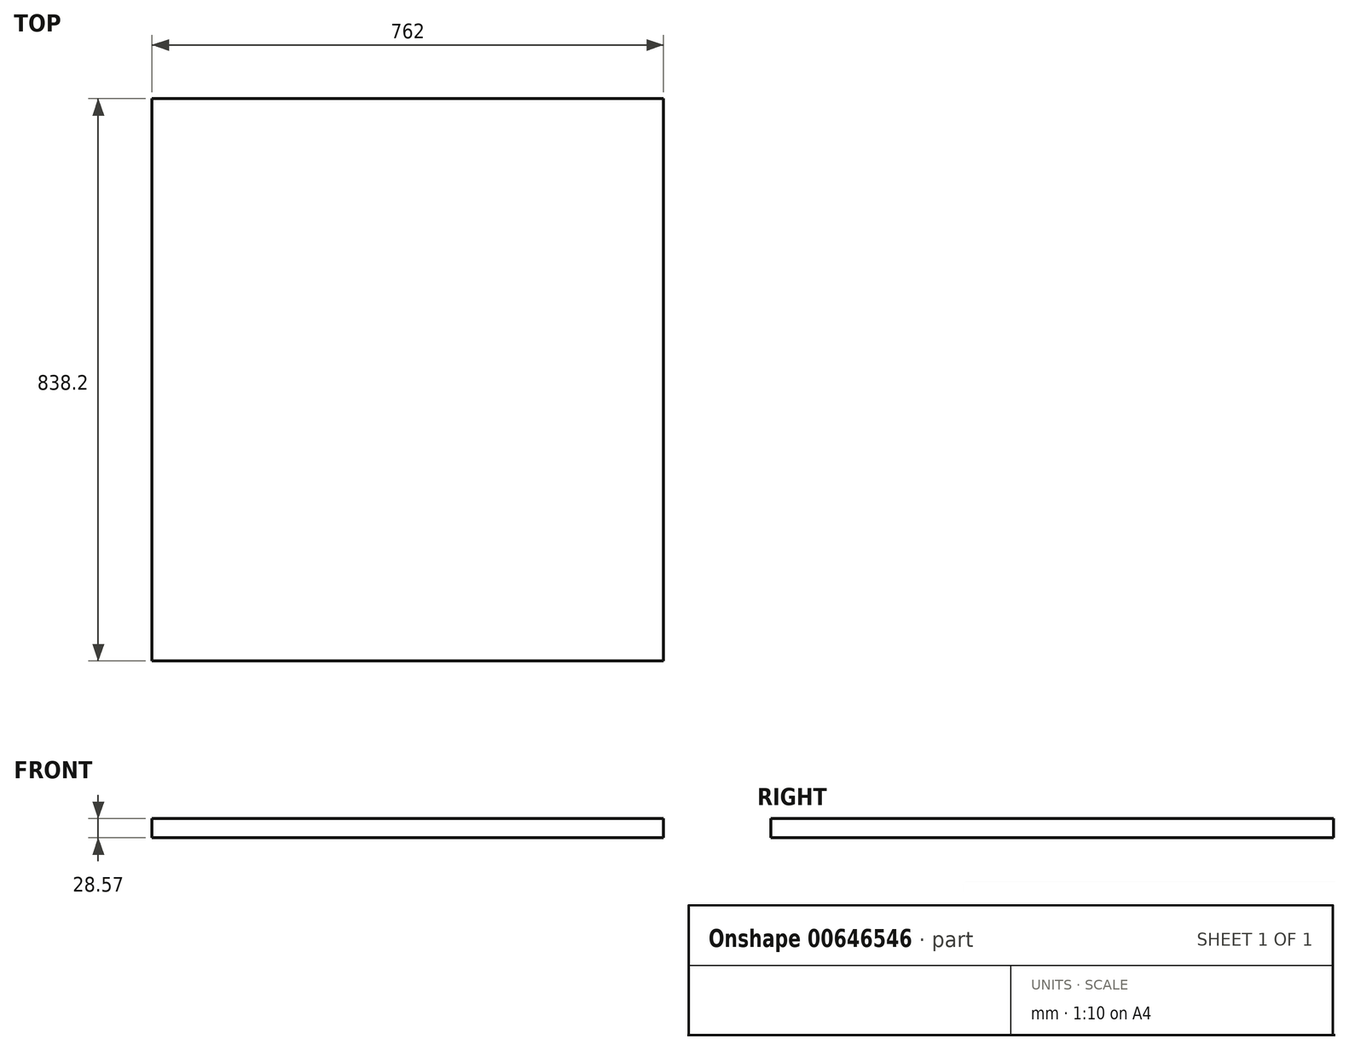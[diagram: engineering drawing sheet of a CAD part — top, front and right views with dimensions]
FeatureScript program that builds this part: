
annotation { "Feature Type Name" : "Feature", "Feature Type Description" : "" }
export const myFeature = defineFeature(function(context is Context, id is Id, definition is map)
    precondition{}
    {
        {
            var Q0;
            Q0=qCreatedBy(makeId("Top.planeOp"),FACE);
            var sketch = newSketch(context, id + "F0", { "sketchPlane" : qUnion([Q0])});
            skLineSegment(sketch, "E0.bottom", {"start": v(381, 419.1) * mm, "end": v(-381, 419.1) * mm});
            skLineSegment(sketch, "E0.top", {"start": v(381, -419.1) * mm, "end": v(-381, -419.1) * mm});
            skLineSegment(sketch, "E0.left", {"start": v(381, 419.1) * mm, "end": v(381, -419.1) * mm});
            skLineSegment(sketch, "E0.right", {"start": v(-381, 419.1) * mm, "end": v(-381, -419.1) * mm});
            skPoint(sketch, "E0.middle", {"position": v(0, 0) * mm});
            skSolve(sketch);
        }
        {
            var Q0;
            Q0=makeQuery(id+"F0.imprint","IMPRINT",FACE,{"disambiguationData":[TD([[makeQuery(id+"F0.imprint","IMPRINT",EDGE,{"derivedFrom":sQuery(id+"F0.wireOp",EDGE,"E0.bottom")}),1.0]])]});
            extrude(context, id + "F1", {"entities" : qUnion([Q0]), "depth" : 28.57 * mm, "offsetDistance" : 25.4 * mm});
        }
    });
